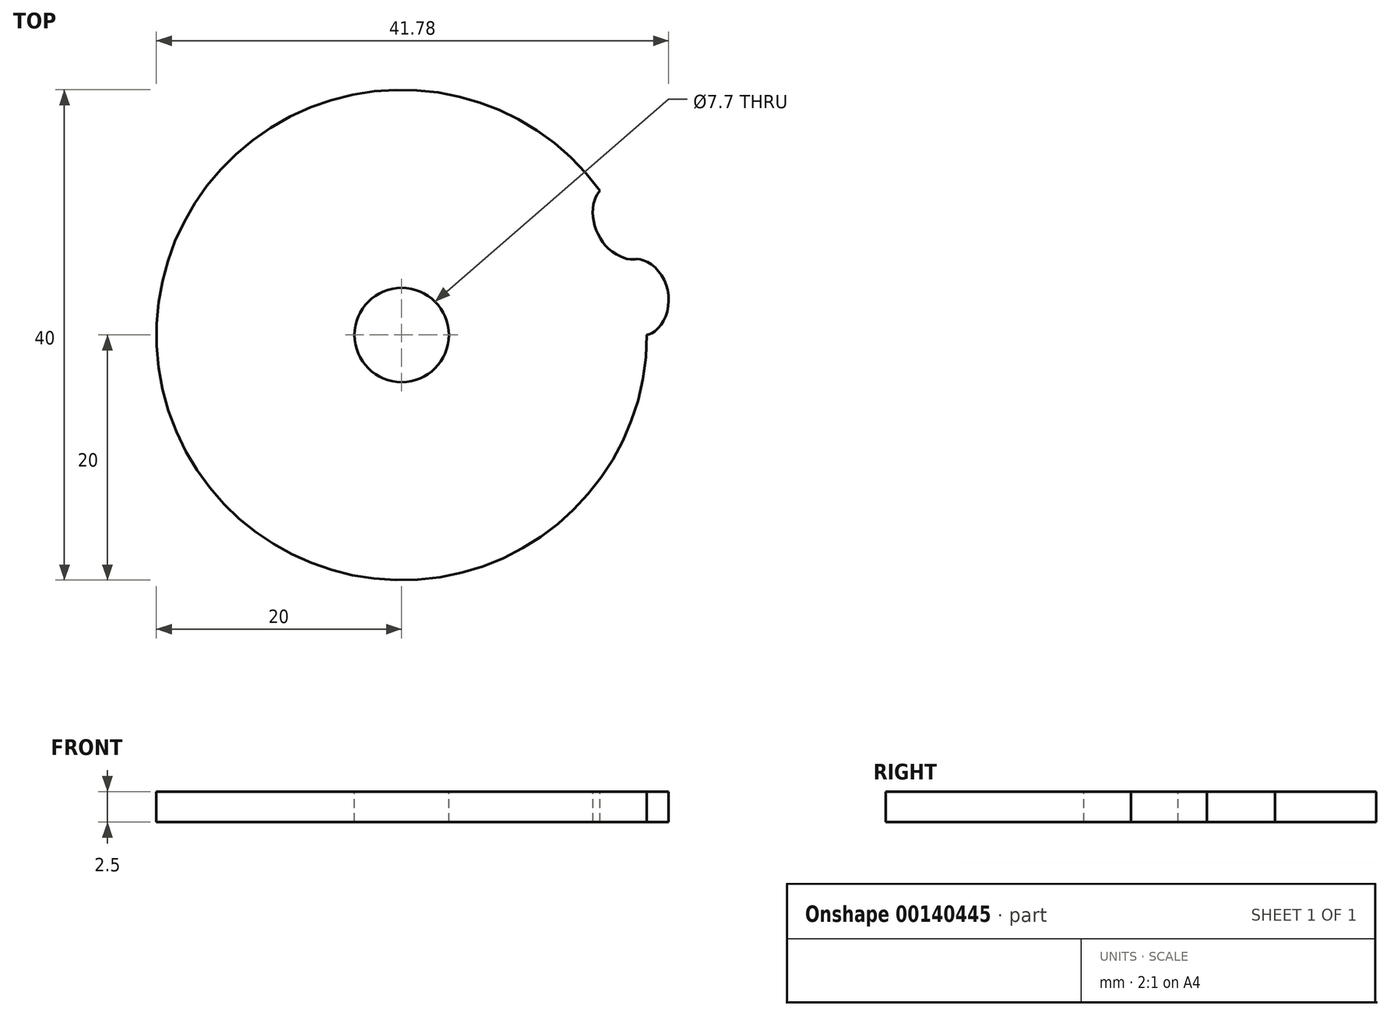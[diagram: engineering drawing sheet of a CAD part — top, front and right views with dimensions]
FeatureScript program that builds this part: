
annotation { "Feature Type Name" : "Feature", "Feature Type Description" : "" }
export const myFeature = defineFeature(function(context is Context, id is Id, definition is map)
    precondition{}
    {
        {
            assignVariable(context, id + "F0", {"name" : "t", "anyValue" : 2.5});
        }
        {
            var Q0;
            Q0=qCreatedBy(makeId("Top.planeOp"),FACE);
            var sketch = newSketch(context, id + "F1", { "sketchPlane" : qUnion([Q0])});
            skCircle(sketch, "E0", {"center": v(0, 0) * mm, "radius": 20 * mm});
            skSolve(sketch);
        }
        {
            var Q0;
            Q0=qSketchRegion(id+"F1",true);
            extrude(context, id + "F2", {"entities" : qUnion([Q0]), "depth" : (getVariable(context, 't')) * mm});
        }
        {
            var Q0;
            Q0=makeQuery(id+"F2.opExtrude","CAP_FACE",FACE,{"disambiguationData":[OSD([sQuery(id+"F1.wireOp",EDGE,"E0")])],"isStart":false});
            var sketch = newSketch(context, id + "F3", { "sketchPlane" : qUnion([Q0])});
            skLineSegment(sketch, "E1", {"start": v(0, 0) * mm, "end": v(19.02, 6.18) * mm, "construction": true});
            skLineSegment(sketch, "E2", {"start": v(19.02, 6.18) * mm, "end": v(20.92, 6.8) * mm, "construction": true});
            skPoint(sketch, "E3", {"position": v(19.97, 6.49) * mm});
            skCircle(sketch, "E4", {"center": v(19.97, 6.49) * mm, "radius": 1 * mm, "construction": true});
            skLineSegment(sketch, "E5", {"start": v(20, 0) * mm, "end": v(21, 0) * mm, "construction": true});
            skLineSegment(sketch, "E6", {"start": v(19.97, 6.49) * mm, "end": v(19.3, 5.75) * mm, "construction": true});
            skLineSegment(sketch, "E7", {"start": v(19.97, 6.49) * mm, "end": v(20.64, 7.23) * mm, "construction": true});
            skLineSegment(sketch, "E8", {"start": v(19.97, 6.49) * mm, "end": v(19, 6.7) * mm, "construction": true});
            skLineSegment(sketch, "E9", {"start": v(19.97, 6.49) * mm, "end": v(20.95, 6.28) * mm, "construction": true});
            skLineSegment(sketch, "E10", {"start": v(19.97, 6.49) * mm, "end": v(19.76, 5.51) * mm, "construction": true});
            skLineSegment(sketch, "E11", {"start": v(19.97, 6.49) * mm, "end": v(20.28, 5.54) * mm, "construction": true});
            skLineSegment(sketch, "E12", {"start": v(19.97, 6.49) * mm, "end": v(20.72, 5.82) * mm, "construction": true});
            skLineSegment(sketch, "E13", {"start": v(19.97, 6.49) * mm, "end": v(20.18, 7.47) * mm, "construction": true});
            skLineSegment(sketch, "E14", {"start": v(19.97, 6.49) * mm, "end": v(19.66, 7.44) * mm, "construction": true});
            skLineSegment(sketch, "E15", {"start": v(19.97, 6.49) * mm, "end": v(19.23, 7.16) * mm, "construction": true});
            skArc(sketch, "E16", {"start": v(21, 0) * mm, "mid": v(20.74, 3.29) * mm, "end": v(19.97, 6.49) * mm, "construction": true});
            skLineSegment(sketch, "E17", {"start": v(20.14, 5.96) * mm, "end": v(0, 0) * mm, "construction": true});
            skLineSegment(sketch, "E18", {"start": v(0, 0) * mm, "end": v(20.28, 5.44) * mm, "construction": true});
            skLineSegment(sketch, "E19", {"start": v(0, 0) * mm, "end": v(20.42, 4.9) * mm, "construction": true});
            skLineSegment(sketch, "E20", {"start": v(0, 0) * mm, "end": v(20.54, 4.37) * mm, "construction": true});
            skLineSegment(sketch, "E21", {"start": v(0, 0) * mm, "end": v(20.65, 3.83) * mm, "construction": true});
            skLineSegment(sketch, "E22", {"start": v(0, 0) * mm, "end": v(20.74, 3.29) * mm, "construction": true});
            skLineSegment(sketch, "E23", {"start": v(0, 0) * mm, "end": v(20.82, 2.74) * mm, "construction": true});
            skLineSegment(sketch, "E24", {"start": v(0, 0) * mm, "end": v(20.88, 2.2) * mm, "construction": true});
            skLineSegment(sketch, "E25", {"start": v(0, 0) * mm, "end": v(20.94, 1.65) * mm, "construction": true});
            skLineSegment(sketch, "E26", {"start": v(0, 0) * mm, "end": v(20.97, 1.1) * mm, "construction": true});
            skLineSegment(sketch, "E27", {"start": v(0, 0) * mm, "end": v(21, 0.55) * mm, "construction": true});
            skLineSegment(sketch, "E28", {"start": v(0, 0) * mm, "end": v(21, 0) * mm, "construction": true});
            skLineSegment(sketch, "E29", {"start": v(21, 0) * mm, "end": v(21.87, 0) * mm, "construction": true});
            skArc(sketch, "E30", {"start": v(19, 6.7) * mm, "mid": v(19.85, 3.4) * mm, "end": v(20.14, 0) * mm, "construction": true});
            skArc(sketch, "E31", {"start": v(19.23, 7.16) * mm, "mid": v(20.2, 3.64) * mm, "end": v(20.52, 0) * mm, "construction": true});
            skArc(sketch, "E32", {"start": v(19.66, 7.44) * mm, "mid": v(20.68, 3.78) * mm, "end": v(21.02, 0) * mm, "construction": true});
            skArc(sketch, "E33", {"start": v(20.18, 7.47) * mm, "mid": v(21.18, 3.8) * mm, "end": v(21.52, 0) * mm, "construction": true});
            skArc(sketch, "E34", {"start": v(20.64, 7.23) * mm, "mid": v(21.56, 3.67) * mm, "end": v(21.87, 0) * mm, "construction": true});
            skPoint(sketch, "E35", {"position": v(19.67, 5.83) * mm});
            skPoint(sketch, "E36", {"position": v(20.14, 5.96) * mm});
            skLineSegment(sketch, "E37", {"start": v(20.14, 5.96) * mm, "end": v(19.16, 6.2) * mm, "construction": true});
            skLineSegment(sketch, "E38", {"start": v(20.28, 5.44) * mm, "end": v(19.58, 6.14) * mm, "construction": true});
            skLineSegment(sketch, "E39", {"start": v(20.42, 4.9) * mm, "end": v(20.19, 5.87) * mm, "construction": true});
            skLineSegment(sketch, "E40", {"start": v(20.54, 4.37) * mm, "end": v(20.85, 5.32) * mm, "construction": true});
            skArc(sketch, "E41", {"start": v(20.92, 6.8) * mm, "mid": v(21.73, 3.44) * mm, "end": v(22, 0) * mm, "construction": true});
            skLineSegment(sketch, "E42", {"start": v(20.65, 3.83) * mm, "end": v(21.4, 4.48) * mm, "construction": true});
            skLineSegment(sketch, "E43", {"start": v(20.74, 3.29) * mm, "end": v(21.73, 3.44) * mm, "construction": true});
            skLineSegment(sketch, "E44", {"start": v(20.82, 2.74) * mm, "end": v(21.74, 2.36) * mm, "construction": true});
            skLineSegment(sketch, "E45", {"start": v(20.88, 2.2) * mm, "end": v(21.47, 1.39) * mm, "construction": true});
            skLineSegment(sketch, "E46", {"start": v(20.94, 1.65) * mm, "end": v(21.01, 0.65) * mm, "construction": true});
            skLineSegment(sketch, "E47", {"start": v(20.97, 1.1) * mm, "end": v(20.52, 0.2) * mm, "construction": true});
            skLineSegment(sketch, "E48", {"start": v(21, 0.55) * mm, "end": v(20.14, 0.03) * mm, "construction": true});
            skFitSpline(sketch, "E49", {"points": [v(19.02, 6.18) * mm, v(19.16, 6.2) * mm, v(19.58, 6.14) * mm, v(20.19, 5.87) * mm, v(20.85, 5.32) * mm, v(21.4, 4.48) * mm, v(21.73, 3.44) * mm, v(21.74, 2.36) * mm, v(21.47, 1.39) * mm, v(21.01, 0.65) * mm, v(20.52, 0.2) * mm, v(20.14, 0.03) * mm, v(20, 0) * mm], "startDerivative": vector(3.64, 1.18) * mm, "endDerivative": vector(-3.82, 0) * mm});
            skArc(sketch, "E50.0", {"start": v(20, 0) * mm, "mid": v(19.75, 3.13) * mm, "end": v(19.02, 6.18) * mm});
            skArc(sketch, "E51", {"start": v(19.02, 6.18) * mm, "mid": v(19.1, 5.93) * mm, "end": v(19.18, 5.68) * mm});
            skArc(sketch, "E52", {"start": v(19.18, 5.68) * mm, "mid": v(19.25, 5.43) * mm, "end": v(19.32, 5.18) * mm});
            skSolve(sketch);
        }
        {
            var Q0;
            Q0=qSketchRegion(id+"F3",true);
            var Q1;
            Q1=makeQuery(id+"F2.opExtrude","CAP_FACE",FACE,{"disambiguationData":[OSD([sQuery(id+"F1.wireOp",EDGE,"E0")])],"isStart":true});
            extrude(context, id + "F4", {"entities" : qUnion([Q0]), "operationType" : NewBodyOperationType.ADD, "endBound" : BoundingType.UP_TO_SURFACE, "oppositeDirection" : true, "endBoundEntityFace" : qUnion([Q1]), "depth" : 2.5 * mm});
        }
        {
            var Q0;
            {var subQ0=sQuery(id+"F3.wireOp",EDGE,"E50.0");Q0=makeQuery(id+"F3.imprint","IMPRINT",FACE,{"disambiguationData":[TD([[makeQuery(id+"F3.imprint","IMPRINT",EDGE,{"derivedFrom":subQ0}),1.0]])]});}
            var sketch = newSketch(context, id + "F5", { "sketchPlane" : qUnion([Q0])});
            skLineSegment(sketch, "E53.0", {"start": v(0, 0) * mm, "end": v(19.02, 6.18) * mm, "construction": true});
            skLineSegment(sketch, "E54.0.0", {"start": v(20, 0) * mm, "end": v(20, 0) * mm});
            skLineSegment(sketch, "E55", {"start": v(0, 0) * mm, "end": v(16.18, 11.76) * mm, "construction": true});
            skCircle(sketch, "E56", {"center": v(15.37, 11.17) * mm, "radius": 1 * mm, "construction": true});
            skArc(sketch, "E57", {"start": v(15.37, 11.17) * mm, "mid": v(16.93, 8.63) * mm, "end": v(18.07, 5.87) * mm, "construction": true});
            skLineSegment(sketch, "E58", {"start": v(15.37, 11.17) * mm, "end": v(15.96, 10.36) * mm, "construction": true});
            skArc(sketch, "E59", {"start": v(15.78, 12.08) * mm, "mid": v(17.6, 9.24) * mm, "end": v(18.9, 6.14) * mm, "construction": true});
            skArc(sketch, "E60", {"start": v(15.27, 12.16) * mm, "mid": v(17.2, 9.25) * mm, "end": v(18.56, 6.03) * mm, "construction": true});
            skArc(sketch, "E61", {"start": v(14.46, 11.57) * mm, "mid": v(16.3, 8.8) * mm, "end": v(17.61, 5.72) * mm, "construction": true});
            skArc(sketch, "E62", {"start": v(14.38, 11.06) * mm, "mid": v(16.05, 8.46) * mm, "end": v(17.25, 5.6) * mm, "construction": true});
            skArc(sketch, "E63", {"start": v(16.18, 11.76) * mm, "mid": v(16.33, 11.54) * mm, "end": v(16.48, 11.33) * mm});
            skLineSegment(sketch, "E64", {"start": v(16.48, 11.33) * mm, "end": v(0, 0) * mm, "construction": true});
            skArc(sketch, "E65", {"start": v(16.18, 11.76) * mm, "mid": v(17.82, 9.08) * mm, "end": v(19.02, 6.18) * mm});
            skLineSegment(sketch, "E66", {"start": v(0, 0) * mm, "end": v(16.77, 10.9) * mm, "construction": true});
            skLineSegment(sketch, "E67", {"start": v(0, 0) * mm, "end": v(17.05, 10.45) * mm, "construction": true});
            skLineSegment(sketch, "E68", {"start": v(0, 0) * mm, "end": v(17.32, 10) * mm, "construction": true});
            skLineSegment(sketch, "E69", {"start": v(0, 0) * mm, "end": v(17.58, 9.54) * mm, "construction": true});
            skLineSegment(sketch, "E70", {"start": v(0, 0) * mm, "end": v(17.82, 9.08) * mm, "construction": true});
            skLineSegment(sketch, "E71", {"start": v(0, 0) * mm, "end": v(18.05, 8.61) * mm, "construction": true});
            skLineSegment(sketch, "E72", {"start": v(0, 0) * mm, "end": v(18.27, 8.13) * mm, "construction": true});
            skLineSegment(sketch, "E73", {"start": v(18.48, 7.65) * mm, "end": v(0, 0) * mm, "construction": true});
            skLineSegment(sketch, "E74", {"start": v(0, 0) * mm, "end": v(18.67, 7.17) * mm, "construction": true});
            skLineSegment(sketch, "E75", {"start": v(0, 0) * mm, "end": v(18.85, 6.68) * mm, "construction": true});
            skLineSegment(sketch, "E76", {"start": v(15.66, 10.76) * mm, "end": v(16.09, 11.66) * mm, "construction": true});
            skLineSegment(sketch, "E77", {"start": v(15.93, 10.35) * mm, "end": v(15.88, 11.35) * mm, "construction": true});
            skArc(sketch, "E78", {"start": v(14.78, 11.98) * mm, "mid": v(16.72, 9.08) * mm, "end": v(18.1, 5.88) * mm, "construction": true});
            skLineSegment(sketch, "E79", {"start": v(16.2, 9.93) * mm, "end": v(15.68, 10.78) * mm, "construction": true});
            skLineSegment(sketch, "E80", {"start": v(16.45, 9.5) * mm, "end": v(15.59, 10) * mm, "construction": true});
            skLineSegment(sketch, "E81", {"start": v(16.7, 9.07) * mm, "end": v(15.7, 9.1) * mm, "construction": true});
            skLineSegment(sketch, "E82", {"start": v(16.93, 8.63) * mm, "end": v(16.04, 8.17) * mm, "construction": true});
            skArc(sketch, "E83", {"start": v(14.56, 10.58) * mm, "mid": v(16.04, 8.17) * mm, "end": v(17.12, 5.56) * mm, "construction": true});
            skLineSegment(sketch, "E84", {"start": v(17.15, 8.18) * mm, "end": v(16.58, 7.36) * mm, "construction": true});
            skLineSegment(sketch, "E85", {"start": v(17.36, 7.73) * mm, "end": v(17.25, 6.73) * mm, "construction": true});
            skLineSegment(sketch, "E86", {"start": v(17.74, 6.8) * mm, "end": v(18.52, 6.18) * mm, "construction": true});
            skLineSegment(sketch, "E87", {"start": v(17.91, 6.34) * mm, "end": v(18.9, 6.16) * mm, "construction": true});
            skFitSpline(sketch, "E88", {"points": [v(19.02, 6.18) * mm, v(18.9, 6.16) * mm, v(18.52, 6.18) * mm, v(17.25, 6.73) * mm, v(16.58, 7.36) * mm, v(16.04, 8.17) * mm, v(15.7, 9.1) * mm, v(15.59, 10) * mm, v(15.68, 10.78) * mm, v(15.88, 11.35) * mm, v(16.09, 11.66) * mm, v(16.18, 11.76) * mm], "startDerivative": vector(-3.44, -1.12) * mm, "endDerivative": vector(2.93, 2.13) * mm});
            skLineSegment(sketch, "E89", {"start": v(15.37, 11.17) * mm, "end": v(15.78, 12.08) * mm, "construction": true});
            skLineSegment(sketch, "E90", {"start": v(15.37, 11.17) * mm, "end": v(15.27, 12.16) * mm, "construction": true});
            skLineSegment(sketch, "E91", {"start": v(15.37, 11.17) * mm, "end": v(14.78, 11.98) * mm, "construction": true});
            skLineSegment(sketch, "E92", {"start": v(15.37, 11.17) * mm, "end": v(14.46, 11.57) * mm, "construction": true});
            skLineSegment(sketch, "E93", {"start": v(15.37, 11.17) * mm, "end": v(14.38, 11.06) * mm, "construction": true});
            skSolve(sketch);
        }
        {
            var Q0;
            Q0=qSketchRegion(id+"F5",true);
            extrude(context, id + "F6", {"entities" : qUnion([Q0]), "operationType" : NewBodyOperationType.REMOVE, "endBound" : BoundingType.THROUGH_ALL, "oppositeDirection" : true, "depth" : 25 * mm});
        }
        {
            var Q0;
            {var subQ0=sQuery(id+"F3.wireOp",EDGE,"E52");var subQ1=sQuery(id+"F3.wireOp",EDGE,"E51");var subQ2=sQuery(id+"F3.wireOp",EDGE,"E50.0");var subQ3=sQuery(id+"F3.wireOp",EDGE,"E49");Q0=makeQuery(id+"FYuu5osC36glpG0_1.29.F4.boolean.opBoolean","MERGE",FACE,{"derivedFrom":[makeQuery(id+"FYuu5osC36glpG0_1.28.F4.boolean.opBoolean","MERGE",FACE,{"derivedFrom":[makeQuery(id+"FYuu5osC36glpG0_1.27.F4.boolean.opBoolean","MERGE",FACE,{"derivedFrom":[makeQuery(id+"FYuu5osC36glpG0_1.26.F4.boolean.opBoolean","MERGE",FACE,{"derivedFrom":[makeQuery(id+"FYuu5osC36glpG0_1.25.F4.boolean.opBoolean","MERGE",FACE,{"derivedFrom":[makeQuery(id+"FYuu5osC36glpG0_1.24.F4.boolean.opBoolean","MERGE",FACE,{"derivedFrom":[makeQuery(id+"FYuu5osC36glpG0_1.23.F4.boolean.opBoolean","MERGE",FACE,{"derivedFrom":[makeQuery(id+"FYuu5osC36glpG0_1.22.F4.boolean.opBoolean","MERGE",FACE,{"derivedFrom":[makeQuery(id+"FYuu5osC36glpG0_1.21.F4.boolean.opBoolean","MERGE",FACE,{"derivedFrom":[makeQuery(id+"FYuu5osC36glpG0_1.20.F4.boolean.opBoolean","MERGE",FACE,{"derivedFrom":[makeQuery(id+"FYuu5osC36glpG0_1.19.F4.boolean.opBoolean","MERGE",FACE,{"derivedFrom":[makeQuery(id+"FYuu5osC36glpG0_1.18.F4.boolean.opBoolean","MERGE",FACE,{"derivedFrom":[makeQuery(id+"FYuu5osC36glpG0_1.17.F4.boolean.opBoolean","MERGE",FACE,{"derivedFrom":[makeQuery(id+"FYuu5osC36glpG0_1.16.F4.boolean.opBoolean","MERGE",FACE,{"derivedFrom":[makeQuery(id+"FYuu5osC36glpG0_1.15.F4.boolean.opBoolean","MERGE",FACE,{"derivedFrom":[makeQuery(id+"FYuu5osC36glpG0_1.14.F4.boolean.opBoolean","MERGE",FACE,{"derivedFrom":[makeQuery(id+"FYuu5osC36glpG0_1.13.F4.boolean.opBoolean","MERGE",FACE,{"derivedFrom":[makeQuery(id+"FYuu5osC36glpG0_1.12.F4.boolean.opBoolean","MERGE",FACE,{"derivedFrom":[makeQuery(id+"FYuu5osC36glpG0_1.11.F4.boolean.opBoolean","MERGE",FACE,{"derivedFrom":[makeQuery(id+"FYuu5osC36glpG0_1.10.F4.boolean.opBoolean","MERGE",FACE,{"derivedFrom":[makeQuery(id+"FYuu5osC36glpG0_1.9.F4.boolean.opBoolean","MERGE",FACE,{"derivedFrom":[makeQuery(id+"FYuu5osC36glpG0_1.8.F4.boolean.opBoolean","MERGE",FACE,{"derivedFrom":[makeQuery(id+"FYuu5osC36glpG0_1.7.F4.boolean.opBoolean","MERGE",FACE,{"derivedFrom":[makeQuery(id+"FYuu5osC36glpG0_1.6.F4.boolean.opBoolean","MERGE",FACE,{"derivedFrom":[makeQuery(id+"FYuu5osC36glpG0_1.5.F4.boolean.opBoolean","MERGE",FACE,{"derivedFrom":[makeQuery(id+"FYuu5osC36glpG0_1.4.F4.boolean.opBoolean","MERGE",FACE,{"derivedFrom":[makeQuery(id+"FYuu5osC36glpG0_1.3.F4.boolean.opBoolean","MERGE",FACE,{"derivedFrom":[makeQuery(id+"FYuu5osC36glpG0_1.2.F4.boolean.opBoolean","MERGE",FACE,{"derivedFrom":[makeQuery(id+"FYuu5osC36glpG0_1.1.F4.boolean.opBoolean","MERGE",FACE,{"derivedFrom":[makeQuery(id+"F4.boolean.opBoolean","MERGE",FACE,{"derivedFrom":[makeQuery(id+"F2.opExtrude","CAP_FACE",FACE,{"disambiguationData":[OSD([sQuery(id+"F1.wireOp",EDGE,"E0")])],"isStart":false}),makeQuery(id+"F4.opExtrude","CAP_FACE",FACE,{"disambiguationData":[OSD([subQ3,subQ2,subQ1,subQ0])],"isStart":true})]}),makeQuery(id+"FYuu5osC36glpG0_1.1.F4.opExtrude","CAP_FACE",FACE,{"disambiguationData":[OSD([subQ3,subQ2,subQ1,subQ0])],"isStart":true})]}),makeQuery(id+"FYuu5osC36glpG0_1.2.F4.opExtrude","CAP_FACE",FACE,{"disambiguationData":[OSD([subQ3,subQ2,subQ1,subQ0])],"isStart":true})]}),makeQuery(id+"FYuu5osC36glpG0_1.3.F4.opExtrude","CAP_FACE",FACE,{"disambiguationData":[OSD([subQ3,subQ2,subQ1,subQ0])],"isStart":true})]}),makeQuery(id+"FYuu5osC36glpG0_1.4.F4.opExtrude","CAP_FACE",FACE,{"disambiguationData":[OSD([subQ3,subQ2,subQ1,subQ0])],"isStart":true})]}),makeQuery(id+"FYuu5osC36glpG0_1.5.F4.opExtrude","CAP_FACE",FACE,{"disambiguationData":[OSD([subQ3,subQ2,subQ1,subQ0])],"isStart":true})]}),makeQuery(id+"FYuu5osC36glpG0_1.6.F4.opExtrude","CAP_FACE",FACE,{"disambiguationData":[OSD([subQ3,subQ2,subQ1,subQ0])],"isStart":true})]}),makeQuery(id+"FYuu5osC36glpG0_1.7.F4.opExtrude","CAP_FACE",FACE,{"disambiguationData":[OSD([subQ3,subQ2,subQ1,subQ0])],"isStart":true})]}),makeQuery(id+"FYuu5osC36glpG0_1.8.F4.opExtrude","CAP_FACE",FACE,{"disambiguationData":[OSD([subQ3,subQ2,subQ1,subQ0])],"isStart":true})]}),makeQuery(id+"FYuu5osC36glpG0_1.9.F4.opExtrude","CAP_FACE",FACE,{"disambiguationData":[OSD([subQ3,subQ2,subQ1,subQ0])],"isStart":true})]}),makeQuery(id+"FYuu5osC36glpG0_1.10.F4.opExtrude","CAP_FACE",FACE,{"disambiguationData":[OSD([subQ3,subQ2,subQ1,subQ0])],"isStart":true})]}),makeQuery(id+"FYuu5osC36glpG0_1.11.F4.opExtrude","CAP_FACE",FACE,{"disambiguationData":[OSD([subQ3,subQ2,subQ1,subQ0])],"isStart":true})]}),makeQuery(id+"FYuu5osC36glpG0_1.12.F4.opExtrude","CAP_FACE",FACE,{"disambiguationData":[OSD([subQ3,subQ2,subQ1,subQ0])],"isStart":true})]}),makeQuery(id+"FYuu5osC36glpG0_1.13.F4.opExtrude","CAP_FACE",FACE,{"disambiguationData":[OSD([subQ3,subQ2,subQ1,subQ0])],"isStart":true})]}),makeQuery(id+"FYuu5osC36glpG0_1.14.F4.opExtrude","CAP_FACE",FACE,{"disambiguationData":[OSD([subQ3,subQ2,subQ1,subQ0])],"isStart":true})]}),makeQuery(id+"FYuu5osC36glpG0_1.15.F4.opExtrude","CAP_FACE",FACE,{"disambiguationData":[OSD([subQ3,subQ2,subQ1,subQ0])],"isStart":true})]}),makeQuery(id+"FYuu5osC36glpG0_1.16.F4.opExtrude","CAP_FACE",FACE,{"disambiguationData":[OSD([subQ3,subQ2,subQ1,subQ0])],"isStart":true})]}),makeQuery(id+"FYuu5osC36glpG0_1.17.F4.opExtrude","CAP_FACE",FACE,{"disambiguationData":[OSD([subQ3,subQ2,subQ1,subQ0])],"isStart":true})]}),makeQuery(id+"FYuu5osC36glpG0_1.18.F4.opExtrude","CAP_FACE",FACE,{"disambiguationData":[OSD([subQ3,subQ2,subQ1,subQ0])],"isStart":true})]}),makeQuery(id+"FYuu5osC36glpG0_1.19.F4.opExtrude","CAP_FACE",FACE,{"disambiguationData":[OSD([subQ3,subQ2,subQ1,subQ0])],"isStart":true})]}),makeQuery(id+"FYuu5osC36glpG0_1.20.F4.opExtrude","CAP_FACE",FACE,{"disambiguationData":[OSD([subQ3,subQ2,subQ1,subQ0])],"isStart":true})]}),makeQuery(id+"FYuu5osC36glpG0_1.21.F4.opExtrude","CAP_FACE",FACE,{"disambiguationData":[OSD([subQ3,subQ2,subQ1,subQ0])],"isStart":true})]}),makeQuery(id+"FYuu5osC36glpG0_1.22.F4.opExtrude","CAP_FACE",FACE,{"disambiguationData":[OSD([subQ3,subQ2,subQ1,subQ0])],"isStart":true})]}),makeQuery(id+"FYuu5osC36glpG0_1.23.F4.opExtrude","CAP_FACE",FACE,{"disambiguationData":[OSD([subQ3,subQ2,subQ1,subQ0])],"isStart":true})]}),makeQuery(id+"FYuu5osC36glpG0_1.24.F4.opExtrude","CAP_FACE",FACE,{"disambiguationData":[OSD([subQ3,subQ2,subQ1,subQ0])],"isStart":true})]}),makeQuery(id+"FYuu5osC36glpG0_1.25.F4.opExtrude","CAP_FACE",FACE,{"disambiguationData":[OSD([subQ3,subQ2,subQ1,subQ0])],"isStart":true})]}),makeQuery(id+"FYuu5osC36glpG0_1.26.F4.opExtrude","CAP_FACE",FACE,{"disambiguationData":[OSD([subQ3,subQ2,subQ1,subQ0])],"isStart":true})]}),makeQuery(id+"FYuu5osC36glpG0_1.27.F4.opExtrude","CAP_FACE",FACE,{"disambiguationData":[OSD([subQ3,subQ2,subQ1,subQ0])],"isStart":true})]}),makeQuery(id+"FYuu5osC36glpG0_1.28.F4.opExtrude","CAP_FACE",FACE,{"disambiguationData":[OSD([subQ3,subQ2,subQ1,subQ0])],"isStart":true})]}),makeQuery(id+"FYuu5osC36glpG0_1.29.F4.opExtrude","CAP_FACE",FACE,{"disambiguationData":[OSD([subQ3,subQ2,subQ1,subQ0])],"isStart":true})]});}
            var sketch = newSketch(context, id + "F7", { "sketchPlane" : qUnion([Q0])});
            skCircle(sketch, "E94", {"center": v(0, 0) * mm, "radius": 3.85 * mm});
            skSolve(sketch);
        }
        {
            var Q0;
            Q0=qSketchRegion(id+"F7",true);
            extrude(context, id + "F8", {"entities" : qUnion([Q0]), "operationType" : NewBodyOperationType.REMOVE, "endBound" : BoundingType.THROUGH_ALL, "oppositeDirection" : true, "depth" : 25 * mm});
        }
    });
